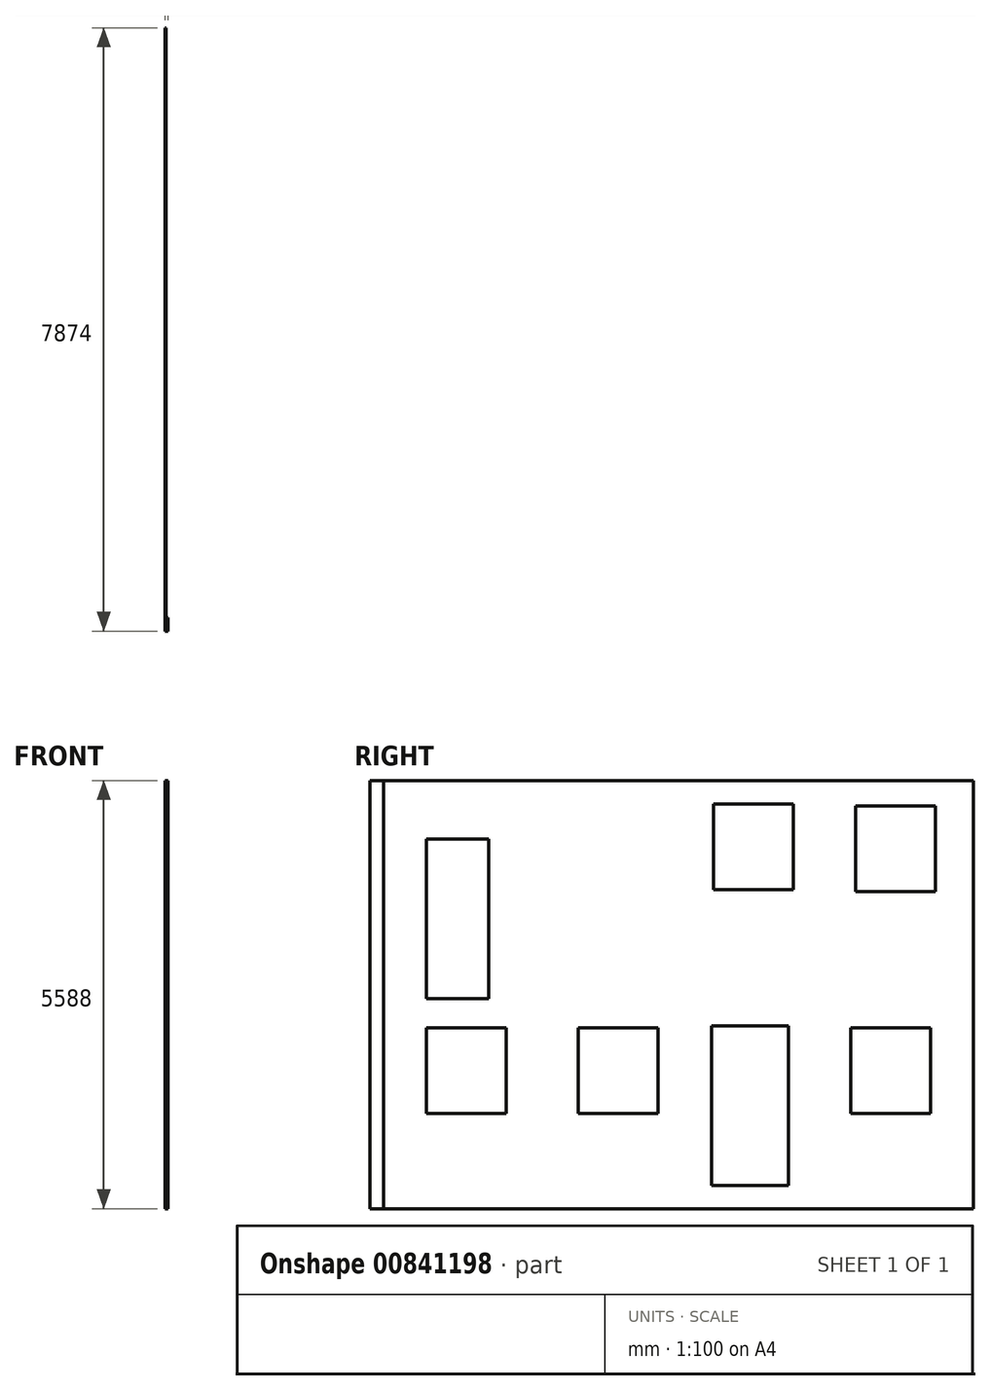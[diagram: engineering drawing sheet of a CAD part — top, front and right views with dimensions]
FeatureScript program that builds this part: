
annotation { "Feature Type Name" : "Feature", "Feature Type Description" : "" }
export const myFeature = defineFeature(function(context is Context, id is Id, definition is map)
    precondition{}
    {
        {
            var Q0;
            Q0=qCreatedBy(makeId("Right.planeOp"),FACE);
            var sketch = newSketch(context, id + "F0", { "sketchPlane" : qUnion([Q0])});
            skLineSegment(sketch, "E0.bottom", {"start": v(0, 0) * mm, "end": v(7874, 0) * mm});
            skLineSegment(sketch, "E0.top", {"start": v(0, 5588) * mm, "end": v(7874, 5588) * mm});
            skLineSegment(sketch, "E0.left", {"start": v(0, 0) * mm, "end": v(0, 5588) * mm});
            skLineSegment(sketch, "E0.right", {"start": v(7874, 0) * mm, "end": v(7874, 5588) * mm});
            skLineSegment(sketch, "E1.bottom", {"start": v(736.6, 2362.2) * mm, "end": v(1778, 2362.2) * mm});
            skLineSegment(sketch, "E1.top", {"start": v(736.6, 1244.6) * mm, "end": v(1778, 1244.6) * mm});
            skLineSegment(sketch, "E1.left", {"start": v(736.6, 2362.2) * mm, "end": v(736.6, 1244.6) * mm});
            skLineSegment(sketch, "E1.right", {"start": v(1778, 2362.2) * mm, "end": v(1778, 1244.6) * mm});
            skLineSegment(sketch, "E2.bottom", {"start": v(2717.8, 2362.2) * mm, "end": v(3759.2, 2362.2) * mm});
            skLineSegment(sketch, "E2.top", {"start": v(2717.8, 1244.6) * mm, "end": v(3759.2, 1244.6) * mm});
            skLineSegment(sketch, "E2.left", {"start": v(2717.8, 2362.2) * mm, "end": v(2717.8, 1244.6) * mm});
            skLineSegment(sketch, "E2.right", {"start": v(3759.2, 2362.2) * mm, "end": v(3759.2, 1244.6) * mm});
            skLineSegment(sketch, "E3.bottom", {"start": v(4457.7, 2387.6) * mm, "end": v(5461, 2387.6) * mm});
            skLineSegment(sketch, "E3.top", {"start": v(4457.7, 304.8) * mm, "end": v(5461, 304.8) * mm});
            skLineSegment(sketch, "E3.left", {"start": v(4457.7, 2387.6) * mm, "end": v(4457.7, 304.8) * mm});
            skLineSegment(sketch, "E3.right", {"start": v(5461, 2387.6) * mm, "end": v(5461, 304.8) * mm});
            skLineSegment(sketch, "E4.bottom", {"start": v(4483.1, 5283.2) * mm, "end": v(5524.5, 5283.2) * mm});
            skLineSegment(sketch, "E4.top", {"start": v(4483.1, 4165.6) * mm, "end": v(5524.5, 4165.6) * mm});
            skLineSegment(sketch, "E4.left", {"start": v(4483.1, 5283.2) * mm, "end": v(4483.1, 4165.6) * mm});
            skLineSegment(sketch, "E4.right", {"start": v(5524.5, 5283.2) * mm, "end": v(5524.5, 4165.6) * mm});
            skLineSegment(sketch, "E5.bottom", {"start": v(6273.8, 2362.2) * mm, "end": v(7315.2, 2362.2) * mm});
            skLineSegment(sketch, "E5.top", {"start": v(6273.8, 1244.6) * mm, "end": v(7315.2, 1244.6) * mm});
            skLineSegment(sketch, "E5.left", {"start": v(6273.8, 2362.2) * mm, "end": v(6273.8, 1244.6) * mm});
            skLineSegment(sketch, "E5.right", {"start": v(7315.2, 2362.2) * mm, "end": v(7315.2, 1244.6) * mm});
            skLineSegment(sketch, "E6.bottom", {"start": v(736.6, 4826) * mm, "end": v(1549.5, 4826) * mm});
            skLineSegment(sketch, "E6.top", {"start": v(736.6, 2743.2) * mm, "end": v(1549.5, 2743.2) * mm});
            skLineSegment(sketch, "E6.left", {"start": v(736.6, 4826) * mm, "end": v(736.6, 2743.2) * mm});
            skLineSegment(sketch, "E6.right", {"start": v(1549.5, 4826) * mm, "end": v(1549.5, 2743.2) * mm});
            skLineSegment(sketch, "E7.bottom", {"start": v(6337.3, 5257.8) * mm, "end": v(7378.7, 5257.8) * mm});
            skLineSegment(sketch, "E7.top", {"start": v(6337.3, 4140.2) * mm, "end": v(7378.7, 4140.2) * mm});
            skLineSegment(sketch, "E7.left", {"start": v(6337.3, 5257.8) * mm, "end": v(6337.3, 4140.2) * mm});
            skLineSegment(sketch, "E7.right", {"start": v(7378.7, 5257.8) * mm, "end": v(7378.7, 4140.2) * mm});
            skSolve(sketch);
        }
        {
            var Q0;
            Q0=makeQuery(id+"F0.imprint","IMPRINT",FACE,{"disambiguationData":[TD([[makeQuery(id+"F0.imprint","IMPRINT",EDGE,{"derivedFrom":sQuery(id+"F0.wireOp",EDGE,"E0.bottom")}),1.0]])]});
            extrude(context, id + "F1", {"entities" : qUnion([Q0]), "depth" : 12.7 * mm, "offsetDistance" : 25.4 * mm});
        }
        {
            var Q0;
            Q0=makeQuery(id+"F1.opExtrude","CAP_FACE",FACE,{"disambiguationData":[OSD([sQuery(id+"F0.wireOp",EDGE,"E0.bottom"),sQuery(id+"F0.wireOp",EDGE,"E0.top"),sQuery(id+"F0.wireOp",EDGE,"E0.left"),sQuery(id+"F0.wireOp",EDGE,"E0.right"),sQuery(id+"F0.wireOp",EDGE,"E1.bottom"),sQuery(id+"F0.wireOp",EDGE,"E1.top"),sQuery(id+"F0.wireOp",EDGE,"E1.left"),sQuery(id+"F0.wireOp",EDGE,"E1.right"),sQuery(id+"F0.wireOp",EDGE,"E2.bottom"),sQuery(id+"F0.wireOp",EDGE,"E2.top"),sQuery(id+"F0.wireOp",EDGE,"E2.left"),sQuery(id+"F0.wireOp",EDGE,"E2.right"),sQuery(id+"F0.wireOp",EDGE,"E3.bottom"),sQuery(id+"F0.wireOp",EDGE,"E3.top"),sQuery(id+"F0.wireOp",EDGE,"E3.left"),sQuery(id+"F0.wireOp",EDGE,"E3.right"),sQuery(id+"F0.wireOp",EDGE,"E4.bottom"),sQuery(id+"F0.wireOp",EDGE,"E4.top"),sQuery(id+"F0.wireOp",EDGE,"E4.left"),sQuery(id+"F0.wireOp",EDGE,"E4.right"),sQuery(id+"F0.wireOp",EDGE,"E5.bottom"),sQuery(id+"F0.wireOp",EDGE,"E5.top"),sQuery(id+"F0.wireOp",EDGE,"E5.left"),sQuery(id+"F0.wireOp",EDGE,"E5.right")])],"isStart":false});
            var sketch = newSketch(context, id + "F2", { "sketchPlane" : qUnion([Q0])});
            skLineSegment(sketch, "E8.bottom", {"start": v(0, 0) * mm, "end": v(177.8, 0) * mm});
            skLineSegment(sketch, "E8.top", {"start": v(0, 5588) * mm, "end": v(177.8, 5588) * mm});
            skLineSegment(sketch, "E8.left", {"start": v(0, 0) * mm, "end": v(0, 5588) * mm});
            skLineSegment(sketch, "E8.right", {"start": v(177.8, 0) * mm, "end": v(177.8, 5588) * mm});
            skSolve(sketch);
        }
        {
            var Q0;
            Q0 = qSketchRegion(id + "F2", true);
            extrude(context, id + "F3", {"entities" : qUnion([Q0]), "operationType" : NewBodyOperationType.ADD, "depth" : 25.4 * mm, "offsetDistance" : 25.4 * mm});
        }
    });
